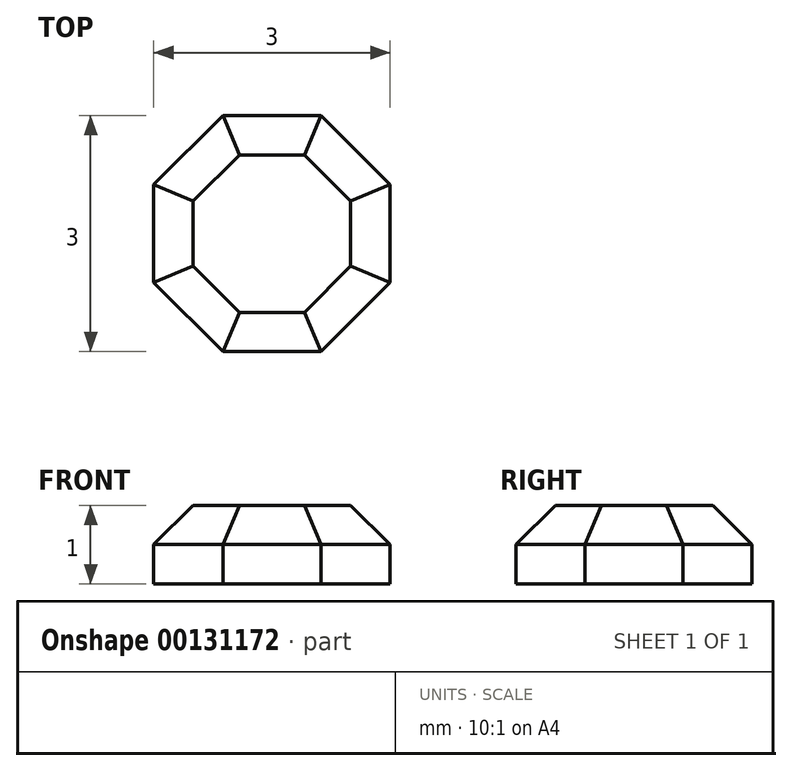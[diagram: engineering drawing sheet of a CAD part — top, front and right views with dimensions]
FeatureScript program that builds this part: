
annotation { "Feature Type Name" : "Feature", "Feature Type Description" : "" }
export const myFeature = defineFeature(function(context is Context, id is Id, definition is map)
    precondition{}
    {
        {
            var Q0;
            Q0=qCreatedBy(makeId("Top.planeOp"),FACE);
            var sketch = newSketch(context, id + "F0", { "sketchPlane" : qUnion([Q0])});
            skCircle(sketch, "E0.cCircle", {"center": v(0, 0) * mm, "radius": 1.5 * mm, "construction": true});
            skLineSegment(sketch, "E0.0", {"start": v(1.5, -0.62) * mm, "end": v(0.62, -1.5) * mm});
            skLineSegment(sketch, "E0.1", {"start": v(0.62, -1.5) * mm, "end": v(-0.62, -1.5) * mm});
            skLineSegment(sketch, "E0.2", {"start": v(-0.62, -1.5) * mm, "end": v(-1.5, -0.62) * mm});
            skLineSegment(sketch, "E0.3", {"start": v(-1.5, -0.62) * mm, "end": v(-1.5, 0.62) * mm});
            skLineSegment(sketch, "E0.4", {"start": v(-1.5, 0.62) * mm, "end": v(-0.62, 1.5) * mm});
            skLineSegment(sketch, "E0.5", {"start": v(-0.62, 1.5) * mm, "end": v(0.62, 1.5) * mm});
            skLineSegment(sketch, "E0.6", {"start": v(0.62, 1.5) * mm, "end": v(1.5, 0.62) * mm});
            skLineSegment(sketch, "E0.7", {"start": v(1.5, 0.62) * mm, "end": v(1.5, -0.62) * mm});
            skPoint(sketch, "E0.0.midPoint", {"position": v(1.06, -1.06) * mm});
            skSolve(sketch);
        }
        {
            var Q0;
            Q0 = qSketchRegion(id + "F0", true);
            extrude(context, id + "F1", {"entities" : qUnion([Q0]), "endBound" : BoundingType.SYMMETRIC, "depth" : 1 * mm});
        }
        {
            var Q0;
            Q0=makeQuery(id+"F1.opExtrude","CAP_FACE",FACE,{"disambiguationData":[OSD([sQuery(id+"F0.wireOp",EDGE,"E0.0"),sQuery(id+"F0.wireOp",EDGE,"E0.1"),sQuery(id+"F0.wireOp",EDGE,"E0.2"),sQuery(id+"F0.wireOp",EDGE,"E0.3"),sQuery(id+"F0.wireOp",EDGE,"E0.4"),sQuery(id+"F0.wireOp",EDGE,"E0.5"),sQuery(id+"F0.wireOp",EDGE,"E0.6"),sQuery(id+"F0.wireOp",EDGE,"E0.7")])],"isStart":false});
            chamfer(context, id + "F2", {"entities" : qUnion([Q0]), "width" : .5 * mm, "tangentPropagation" : true});
        }
    });
